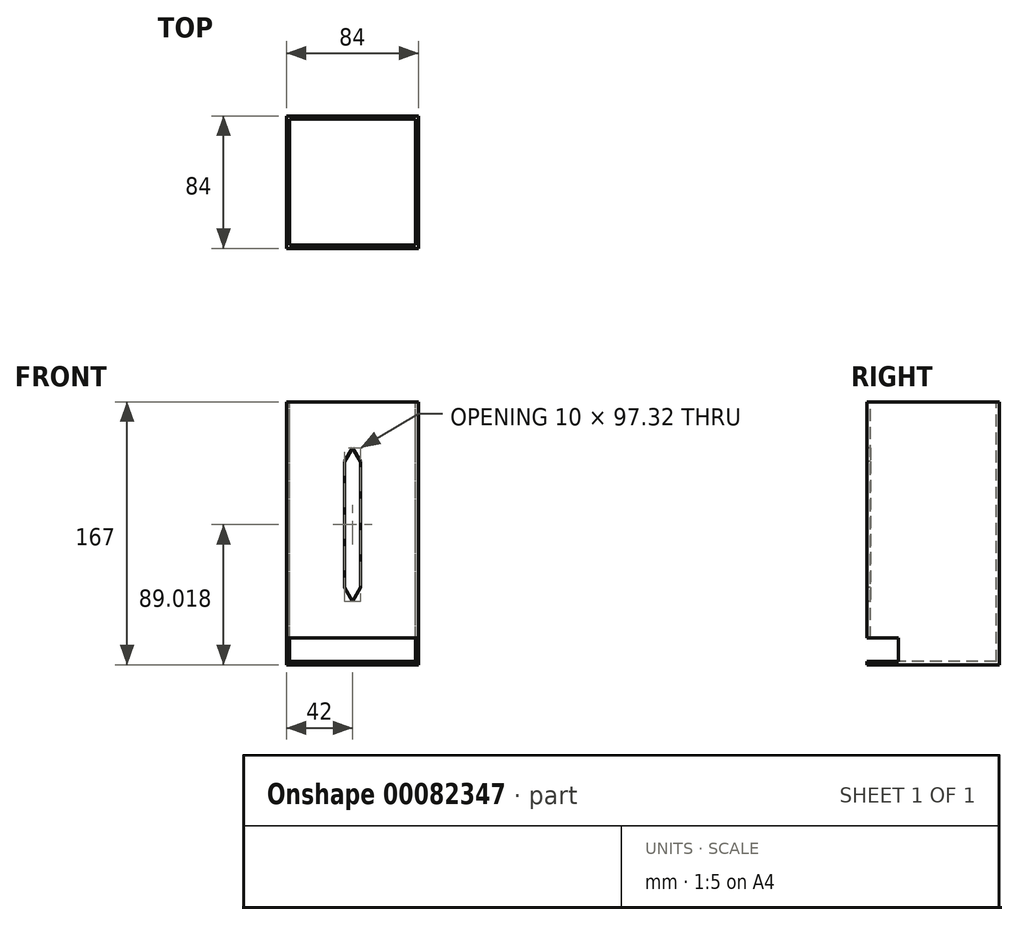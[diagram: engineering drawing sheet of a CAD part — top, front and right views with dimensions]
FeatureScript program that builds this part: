
annotation { "Feature Type Name" : "Feature", "Feature Type Description" : "" }
export const myFeature = defineFeature(function(context is Context, id is Id, definition is map)
    precondition{}
    {
        {
            var Q0;
            Q0=qCreatedBy(makeId("Top.planeOp"),FACE);
            var sketch = newSketch(context, id + "F0", { "sketchPlane" : qUnion([Q0])});
            skLineSegment(sketch, "E0.bottom", {"start": v(-42, 42) * mm, "end": v(42, 42) * mm});
            skLineSegment(sketch, "E0.top", {"start": v(-42, -42) * mm, "end": v(42, -42) * mm});
            skLineSegment(sketch, "E0.left", {"start": v(-42, 42) * mm, "end": v(-42, -42) * mm});
            skLineSegment(sketch, "E0.right", {"start": v(42, 42) * mm, "end": v(42, -42) * mm});
            skPoint(sketch, "E0.middle", {"position": v(0, 0) * mm});
            skSolve(sketch);
        }
        {
            var Q0;
            Q0 = qSketchRegion(id + "F0", true);
            extrude(context, id + "F1", {"entities" : qUnion([Q0]), "depth" : 167 * mm});
        }
        {
            var Q0;
            Q0=makeQuery(id+"F1.opExtrude","CAP_FACE",FACE,{"disambiguationData":[OSD([sQuery(id+"F0.wireOp",EDGE,"E0.bottom"),sQuery(id+"F0.wireOp",EDGE,"E0.top"),sQuery(id+"F0.wireOp",EDGE,"E0.left"),sQuery(id+"F0.wireOp",EDGE,"E0.right")])],"isStart":false});
            var sketch = newSketch(context, id + "F2", { "sketchPlane" : qUnion([Q0])});
            skLineSegment(sketch, "E1.bottom", {"start": v(-40, 40) * mm, "end": v(40, 40) * mm});
            skLineSegment(sketch, "E1.top", {"start": v(-40, -40) * mm, "end": v(40, -40) * mm});
            skLineSegment(sketch, "E1.left", {"start": v(-40, 40) * mm, "end": v(-40, -40) * mm});
            skLineSegment(sketch, "E1.right", {"start": v(40, 40) * mm, "end": v(40, -40) * mm});
            skPoint(sketch, "E1.middle", {"position": v(0, 0) * mm});
            skSolve(sketch);
        }
        {
            var Q0;
            Q0=makeQuery(id+"F2.imprint","IMPRINT",FACE,{"disambiguationData":[TD([[makeQuery(id+"F2.imprint","IMPRINT",EDGE,{"derivedFrom":sQuery(id+"F2.wireOp",EDGE,"E1.bottom")}),-1.0]])]});
            extrude(context, id + "F3", {"entities" : qUnion([Q0]), "operationType" : NewBodyOperationType.REMOVE, "oppositeDirection" : true, "depth" : 165 * mm});
        }
        {
            var Q0;
            Q0=makeQuery(id+"F1.opExtrude","SWEPT_FACE",FACE,{"disambiguationData":[OSD([sQuery(id+"F0.wireOp",EDGE,"E0.right")])]});
            var sketch = newSketch(context, id + "F4", { "sketchPlane" : qUnion([Q0])});
            skLineSegment(sketch, "E2.bottom", {"start": v(-42, 17) * mm, "end": v(-22, 17) * mm});
            skLineSegment(sketch, "E2.top", {"start": v(-42, 2) * mm, "end": v(-22, 2) * mm});
            skLineSegment(sketch, "E2.left", {"start": v(-42, 17) * mm, "end": v(-42, 2) * mm});
            skLineSegment(sketch, "E2.right", {"start": v(-22, 17) * mm, "end": v(-22, 2) * mm});
            skSolve(sketch);
        }
        {
            var Q0;
            Q0=makeQuery(id+"F4.imprint","IMPRINT",FACE,{"disambiguationData":[TD([[makeQuery(id+"F4.imprint","IMPRINT",EDGE,{"derivedFrom":sQuery(id+"F4.wireOp",EDGE,"E2.bottom")}),-1.0]])]});
            extrude(context, id + "F5", {"entities" : qUnion([Q0]), "operationType" : NewBodyOperationType.REMOVE, "oppositeDirection" : true, "depth" : 84 * mm});
        }
        {
            var Q0;
            {var subQ2=sQuery(id+"F0.wireOp",EDGE,"E0.top");Q0=makeQuery(id+"F5.boolean.opBoolean","SPLIT",FACE,{"disambiguationData":[TD([makeQuery(id+"F5.opExtrude","SWEPT_FACE",FACE,{"disambiguationData":[OSD([sQuery(id+"F4.wireOp",EDGE,"E2.bottom")])]})])],"derivedFrom":makeQuery(id+"F1.opExtrude","SWEPT_FACE",FACE,{"disambiguationData":[OSD([subQ2])]})});}
            var sketch = newSketch(context, id + "F6", { "sketchPlane" : qUnion([Q0])});
            skLineSegment(sketch, "E3.bottom", {"start": v(-5, 129.02) * mm, "end": v(5, 129.02) * mm});
            skLineSegment(sketch, "E3.top", {"start": v(-5, 49.02) * mm, "end": v(5, 49.02) * mm});
            skLineSegment(sketch, "E3.left", {"start": v(-5, 129.02) * mm, "end": v(-5, 49.02) * mm});
            skLineSegment(sketch, "E3.right", {"start": v(5, 129.02) * mm, "end": v(5, 49.02) * mm});
            skPoint(sketch, "E3.middle", {"position": v(0, 89.02) * mm});
            skLineSegment(sketch, "E4", {"start": v(-5, 129.02) * mm, "end": v(0, 137.68) * mm});
            skLineSegment(sketch, "E5", {"start": v(0, 137.68) * mm, "end": v(5, 129.02) * mm});
            skLineSegment(sketch, "E6", {"start": v(-5, 49.02) * mm, "end": v(0, 40.36) * mm});
            skLineSegment(sketch, "E7", {"start": v(0, 40.36) * mm, "end": v(5, 49.02) * mm});
            skSolve(sketch);
        }
        {
            var Q0;
            Q0=makeQuery(id+"F6.imprint","IMPRINT",FACE,{"disambiguationData":[TD([[makeQuery(id+"F6.imprint","IMPRINT",EDGE,{"derivedFrom":sQuery(id+"F6.wireOp",EDGE,"E3.top")}),-1.0]])]});
            var Q1;
            Q1=makeQuery(id+"F6.imprint","IMPRINT",FACE,{"disambiguationData":[TD([[makeQuery(id+"F6.imprint","IMPRINT",EDGE,{"derivedFrom":sQuery(id+"F6.wireOp",EDGE,"E3.bottom")}),-1.0]])]});
            var Q2;
            Q2=makeQuery(id+"F6.imprint","IMPRINT",FACE,{"disambiguationData":[TD([[makeQuery(id+"F6.imprint","IMPRINT",EDGE,{"derivedFrom":sQuery(id+"F6.wireOp",EDGE,"E3.bottom")}),1.0]])]});
            extrude(context, id + "F7", {"entities" : qUnion([Q0, Q1, Q2]), "operationType" : NewBodyOperationType.REMOVE, "oppositeDirection" : true, "depth" : 2 * mm});
        }
    });
